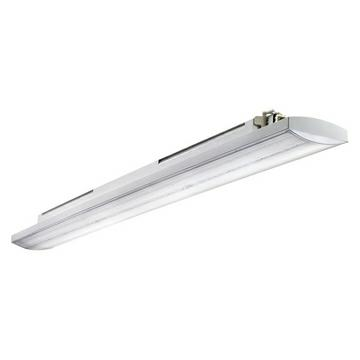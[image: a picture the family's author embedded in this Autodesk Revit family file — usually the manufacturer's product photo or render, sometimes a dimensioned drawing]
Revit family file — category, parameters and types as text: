
# Revit family: Lighting-Industrial-GEWISS-SMART[3]PLUS-WATERTIGHT-LED_TRANSPARENT_1600mm
name_source: partatom
category: Apparecchi per illuminazione
units: mm (PartAtom-declared; Revit-internal decimal feet)

## family parameters
Condiviso = No
Host = Superficie
Punto di calcolo locali = No
Quota connettore circolare = Usa diametro
Sorgente d'illuminazione = Sì
Taglio con vuoti quando caricato = No
Tipo di parte = Normale

## types (1)
- Lighting-Industrial-GEWISS-SMART[3]PLUS-WATERTIGHT-LED_TRANSPARENT_1600mm
    Angolo inclinazione = -90.00°
    Application = Indoor
    Carico apparente = 67 VA
    Catalogue = LIGHTING
    Catalogue Range = SMART[3] PLUS
    Colour temperature = 5700 K (CRI > 90)
    Colour temperature: = 5700 K (CRI > 90)
    Commenti sul wattaggio = 67W
    Descrizione = SMART3 PLUS 1600 T.W.DALI HE TRASP 9 57
    Efficiency class of integrated LEDs = A ÷ A++
    Electrocod = 2434
    Emetti da lunghezza linea = 1200 mm
    File diagramma fotometrico = GWS3323AT957.IES
    Filtro dei colori = 16777215
    Ganci = Alluminio
    Glow Wire Test = 850°C
    IDF = 012ff93d-6ea3-4203-a83f-40d6eaab17c7
    IDT = 5236158c-1d15-421c-8690-1b1aa3a85baf
    IP degree = IP66/IP69
    Immagine tipo = GWS3280TS.jpg
    Insulation class = II
    Lamp = LED
    Lampada = LED
    Length = 1600 mm
    Lumen output (lm) = 5900
    Lunghezza Lampada = 1600 mm  [stored 5.24934 ft]
    Modello = GWS3323AT957
    Numero poli = 2
    Operating temperature: = -25 +50 °C
    Produttore = GEWISS S.p.A.
    Prospetto di default = 1219 mm
    SEO = Ceiling
    Schermo. = Led Acceso
    Shield type = Transparent
    Shock resistance = IK08
    Stampa 1_100 = Sì
    Stampa 1_200 = No
    Struttura = GRIGIO
    System power = 50 W
    Technical sheet = https://www.gewiss.com
    Type of light source = LED - Not replaceable
    Typology = DALI
    URL = https://www.gewiss.com
    Variazione temperatura colore lampada con luminosità attenuata = <Nessuno>
    Version file RFA = 20.0
    Voltage = 220-240 V
    Warranty = 5 years
    Working temperature = -25 +50 °C

note: [stored X ft] marks values corroborated as IEEE doubles in the binary element streams (Revit-internal decimal feet)
